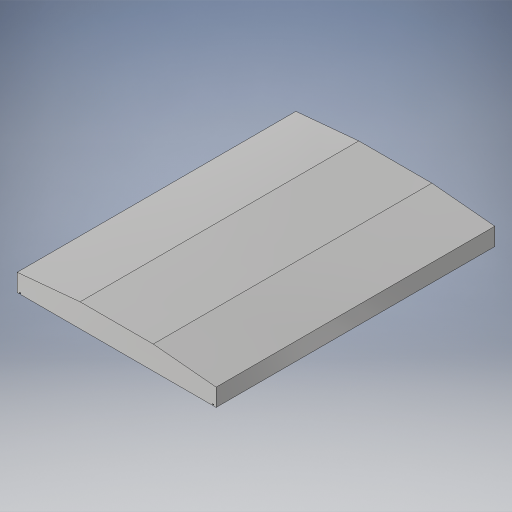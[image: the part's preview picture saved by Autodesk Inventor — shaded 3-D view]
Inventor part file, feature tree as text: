
AUTODESK INVENTOR PART (.ipt)
format: ipt  version: 2023.2 (Build 272271000, 271)  size: 271,360 bytes
history: native  units: in
note: dims shown in document units (in); Inventor stores cm internally (conversion verified against a paired STEP export)
features: extrude x1, sketch x1, projected_geometry x1
ambient origin geometry x8: Origin, YZ Plane, XZ Plane, XY Plane, X Axis, Y Axis, Z Axis, Center Point
bodies: Solid1 (feature_tree)
feature tree (3):
  extrude  "Extrusion1"  Depth=0.375in
  sketch  "Sketch2"  dims[d3=0.375in d4=0.375in d5=0.25in d6=0.25in d7=0.25in d8=0.0in]
  projected_geometry  "Projected Loop1"
